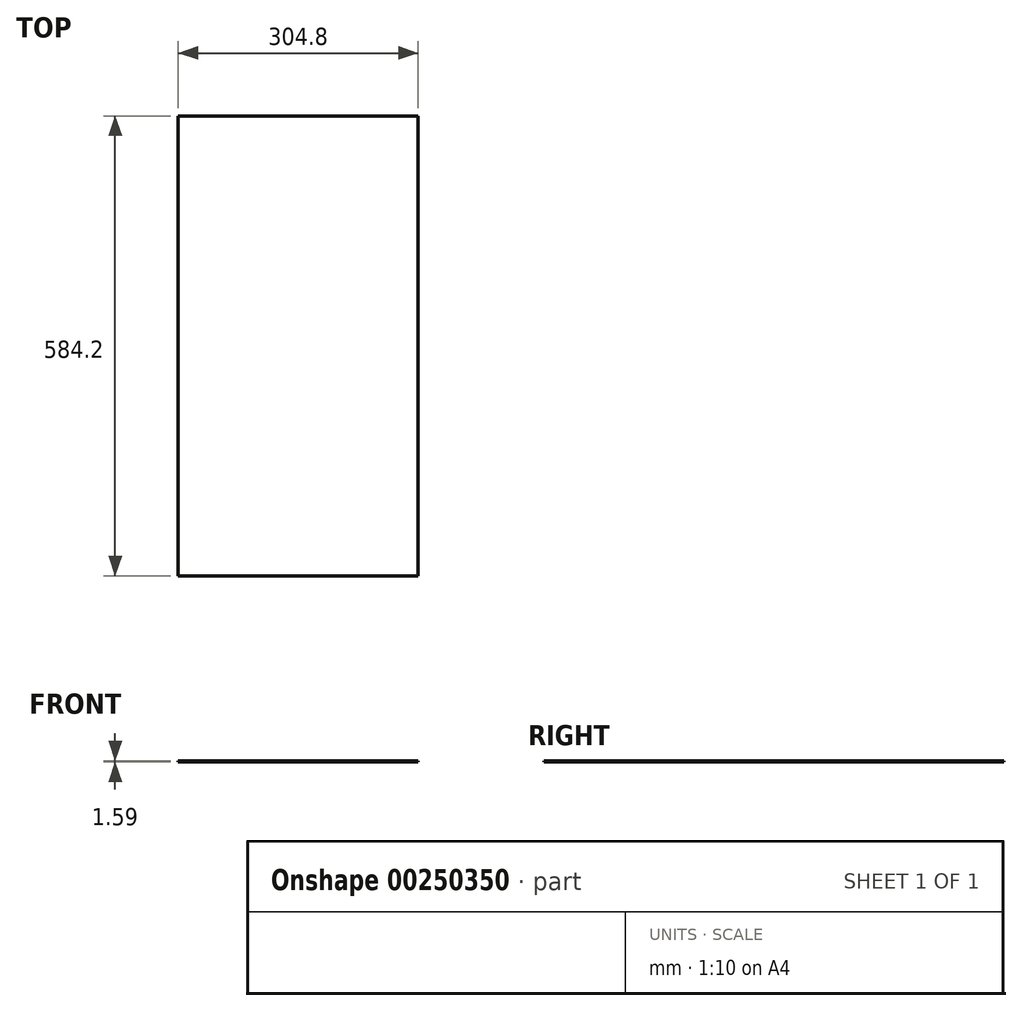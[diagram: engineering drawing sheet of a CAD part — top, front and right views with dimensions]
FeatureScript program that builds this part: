
annotation { "Feature Type Name" : "Feature", "Feature Type Description" : "" }
export const myFeature = defineFeature(function(context is Context, id is Id, definition is map)
    precondition{}
    {
        {
            var Q0;
            Q0=qCreatedBy(makeId("Top.planeOp"),FACE);
            var sketch = newSketch(context, id + "F0", { "sketchPlane" : qUnion([Q0])});
            skLineSegment(sketch, "E0.bottom", {"start": v(152.4, 292.1) * mm, "end": v(-152.4, 292.1) * mm});
            skLineSegment(sketch, "E0.top", {"start": v(152.4, -292.1) * mm, "end": v(-152.4, -292.1) * mm});
            skLineSegment(sketch, "E0.left", {"start": v(152.4, 292.1) * mm, "end": v(152.4, -292.1) * mm});
            skLineSegment(sketch, "E0.right", {"start": v(-152.4, 292.1) * mm, "end": v(-152.4, -292.1) * mm});
            skPoint(sketch, "E0.middle", {"position": v(0, 0) * mm});
            skSolve(sketch);
        }
        {
            var Q0;
            Q0 = qSketchRegion(id + "F0", true);
            extrude(context, id + "F1", {"entities" : qUnion([Q0]), "depth" : 1.59 * mm});
        }
    });
